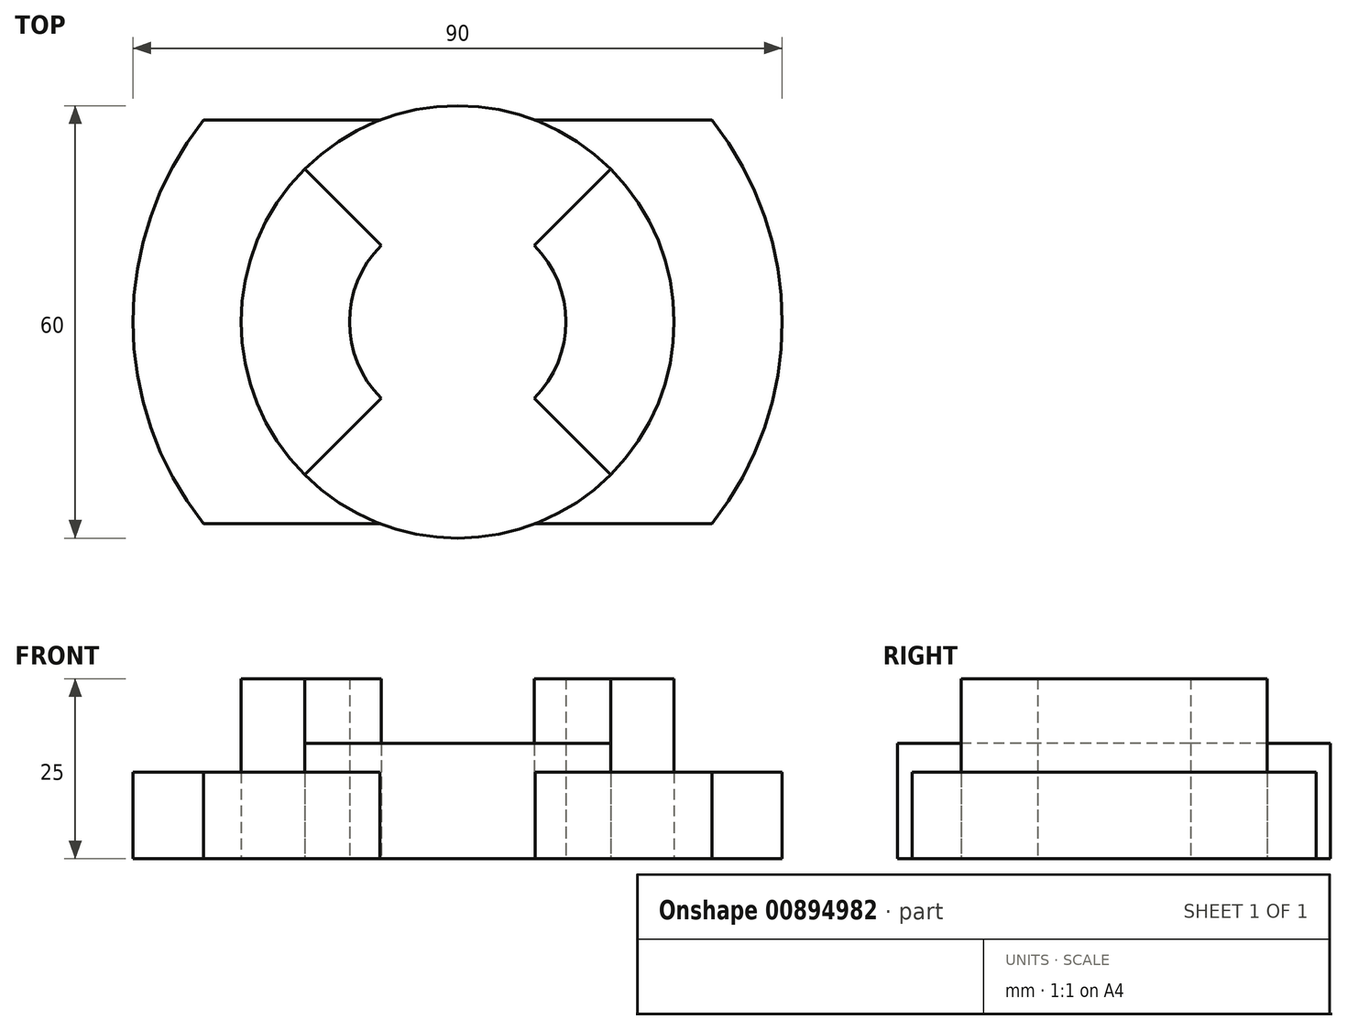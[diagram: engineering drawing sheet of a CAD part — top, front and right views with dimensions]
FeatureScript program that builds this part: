
annotation { "Feature Type Name" : "Feature", "Feature Type Description" : "" }
export const myFeature = defineFeature(function(context is Context, id is Id, definition is map)
    precondition{}
    {
        {
            var Q0;
            Q0=qCreatedBy(makeId("Top.planeOp"),FACE);
            var sketch = newSketch(context, id + "F0", { "sketchPlane" : qUnion([Q0])});
            skCircle(sketch, "E0", {"center": v(0, 0) * mm, "radius": 30 * mm});
            skArc(sketch, "E1", {"start": v(-35.23, 28) * mm, "mid": v(-45, 0) * mm, "end": v(-35.23, -28) * mm});
            skLineSegment(sketch, "E2", {"start": v(35.23, -28) * mm, "end": v(10.77, -28) * mm});
            skLineSegment(sketch, "E3", {"start": v(35.23, 28) * mm, "end": v(10.77, 28) * mm});
            skLineSegment(sketch, "E4.trimOffspring", {"start": v(-10.77, 28) * mm, "end": v(-35.23, 28) * mm});
            skLineSegment(sketch, "E5.trimOffspring", {"start": v(-10.77, -28) * mm, "end": v(-35.23, -28) * mm});
            skArc(sketch, "E6.trimOffspring", {"start": v(35.23, -28) * mm, "mid": v(45, 0) * mm, "end": v(35.23, 28) * mm});
            skLineSegment(sketch, "E7", {"start": v(-21.21, 21.21) * mm, "end": v(-10.6, 10.6) * mm});
            skLineSegment(sketch, "E8", {"start": v(21.21, 21.21) * mm, "end": v(10.6, 10.6) * mm});
            skArc(sketch, "E9", {"start": v(-10.6, 10.6) * mm, "mid": v(-15, 0) * mm, "end": v(-10.6, -10.6) * mm});
            skLineSegment(sketch, "E10.trimOffspring", {"start": v(10.6, -10.6) * mm, "end": v(21.21, -21.21) * mm});
            skLineSegment(sketch, "E11.trimOffspring", {"start": v(-10.6, -10.6) * mm, "end": v(-21.21, -21.21) * mm});
            skArc(sketch, "E12.trimOffspring", {"start": v(10.6, -10.6) * mm, "mid": v(15, 0) * mm, "end": v(10.6, 10.6) * mm});
            skSolve(sketch);
        }
        {
            var Q0;
            Q0=makeQuery(id+"F0.imprint","IMPRINT",FACE,{"disambiguationData":[TD([[makeQuery(id+"F0.imprint","IMPRINT",EDGE,{"derivedFrom":sQuery(id+"F0.wireOp",EDGE,"E1")}),1.0]])]});
            var Q1;
            {var subQ0=sQuery(id+"F0.wireOp",EDGE,"E2");Q1=makeQuery(id+"F0.imprint","IMPRINT",FACE,{"disambiguationData":[TD([[makeQuery(id+"F0.imprint","IMPRINT",EDGE,{"derivedFrom":subQ0}),-1.0]])]});}
            extrude(context, id + "F1", {"entities" : qUnion([Q0, Q1]), "depth" : 12 * mm, "offsetDistance" : 25 * mm});
        }
        {
            var Q0;
            {var subQ0=sQuery(id+"F0.wireOp",EDGE,"E0");var subQ1=makeQuery(id+"F0.imprint","INTERSECT",VERTEX,{"derivedFrom":[subQ0,sQuery(id+"F0.wireOp",EDGE,"E3")]});Q0=makeQuery(id+"F0.imprint","IMPRINT",FACE,{"disambiguationData":[TD([[makeQuery(id+"F0.imprint","IMPRINT",EDGE,{"disambiguationData":[TD([[subQ1,-1.0]])],"derivedFrom":subQ0}),1.0]])]});}
            extrude(context, id + "F2", {"entities" : qUnion([Q0]), "depth" : 16 * mm, "offsetDistance" : 25 * mm});
        }
        {
            var Q0;
            {var subQ0=sQuery(id+"F0.wireOp",EDGE,"E8");Q0=makeQuery(id+"F0.imprint","IMPRINT",FACE,{"disambiguationData":[TD([[makeQuery(id+"F0.imprint","IMPRINT",EDGE,{"derivedFrom":subQ0}),1.0]])]});}
            var Q1;
            {var subQ0=sQuery(id+"F0.wireOp",EDGE,"E7");Q1=makeQuery(id+"F0.imprint","IMPRINT",FACE,{"disambiguationData":[TD([[makeQuery(id+"F0.imprint","IMPRINT",EDGE,{"derivedFrom":subQ0}),-1.0]])]});}
            extrude(context, id + "F3", {"entities" : qUnion([Q0, Q1]), "depth" : 25 * mm, "offsetDistance" : 25 * mm});
        }
    });
